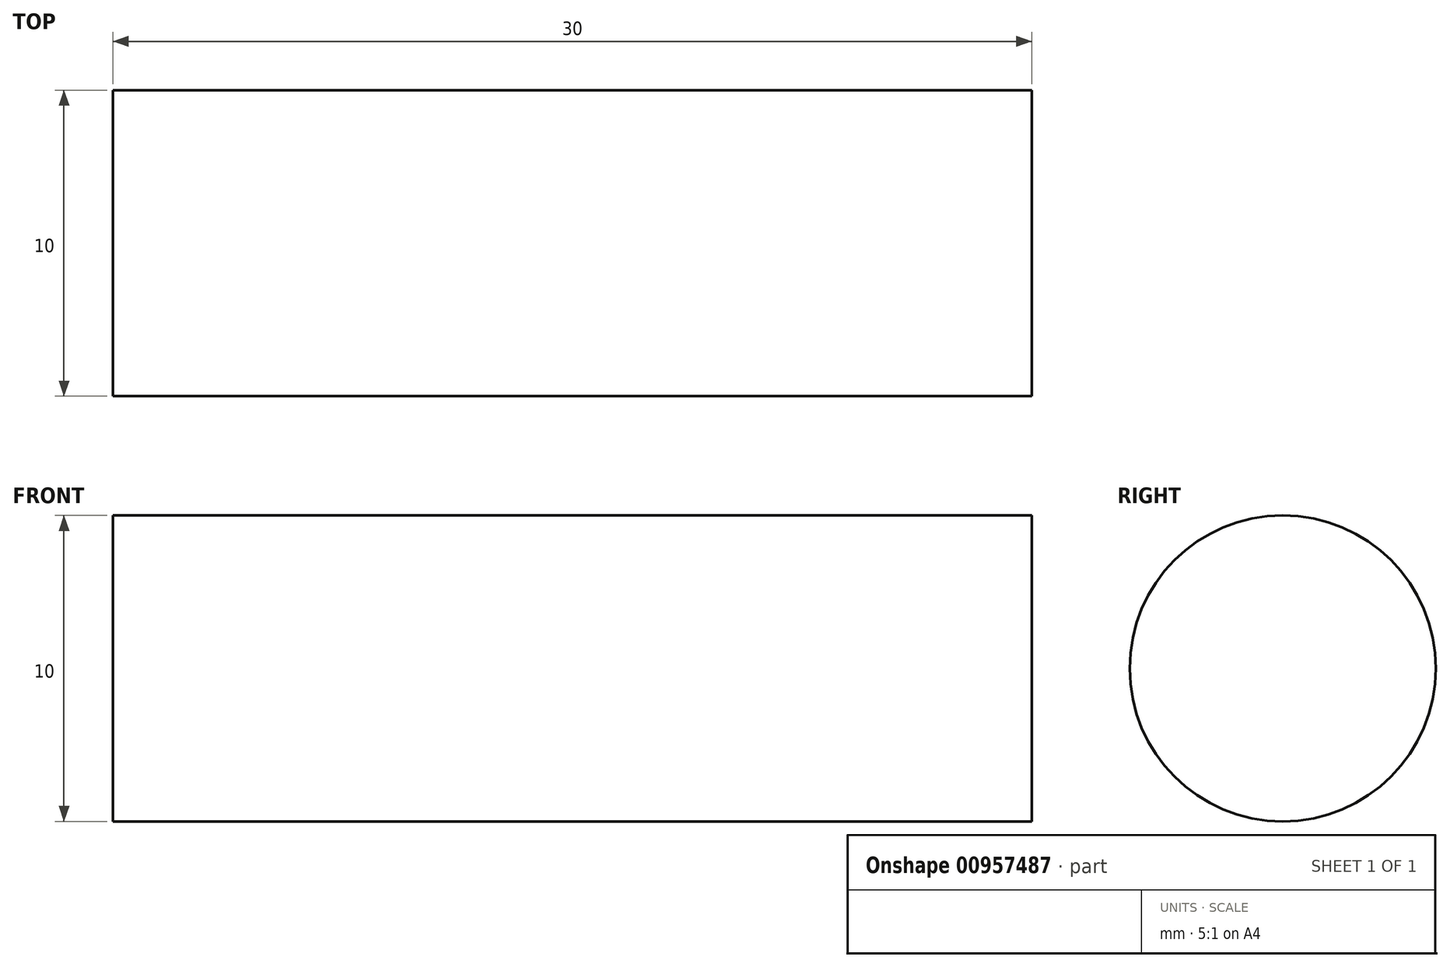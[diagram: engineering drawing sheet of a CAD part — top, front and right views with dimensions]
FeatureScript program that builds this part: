
annotation { "Feature Type Name" : "Feature", "Feature Type Description" : "" }
export const myFeature = defineFeature(function(context is Context, id is Id, definition is map)
    precondition{}
    {
        {
            var Q0;
            Q0=qCreatedBy(makeId("Front.planeOp"),FACE);
            var sketch = newSketch(context, id + "F0", { "sketchPlane" : qUnion([Q0])});
            skLineSegment(sketch, "E0", {"start": v(0, 0) * mm, "end": v(-30, 0) * mm});
            skLineSegment(sketch, "E1", {"start": v(-30, 0) * mm, "end": v(-30, 5) * mm});
            skLineSegment(sketch, "E2", {"start": v(-30, 5) * mm, "end": v(0, 5) * mm});
            skLineSegment(sketch, "E3", {"start": v(0, 5) * mm, "end": v(0, 0) * mm});
            skSolve(sketch);
        }
        {
            var Q0;
            Q0=makeQuery(id+"F0.imprint","IMPRINT",FACE,{"disambiguationData":[TD([[makeQuery(id+"F0.imprint","IMPRINT",EDGE,{"derivedFrom":sQuery(id+"F0.wireOp",EDGE,"E0")}),-1.0]])]});
            var Q1;
            Q1=sQuery(id+"F0.wireOp",EDGE,"E0");
            revolve(context, id + "F1", {"surfaceOperationType" : NewSurfaceOperationType.NEW, "entities" : qUnion([Q0]), "axis" : qUnion([Q1]), "revolveType" : RevolveType.FULL});
        }
    });
